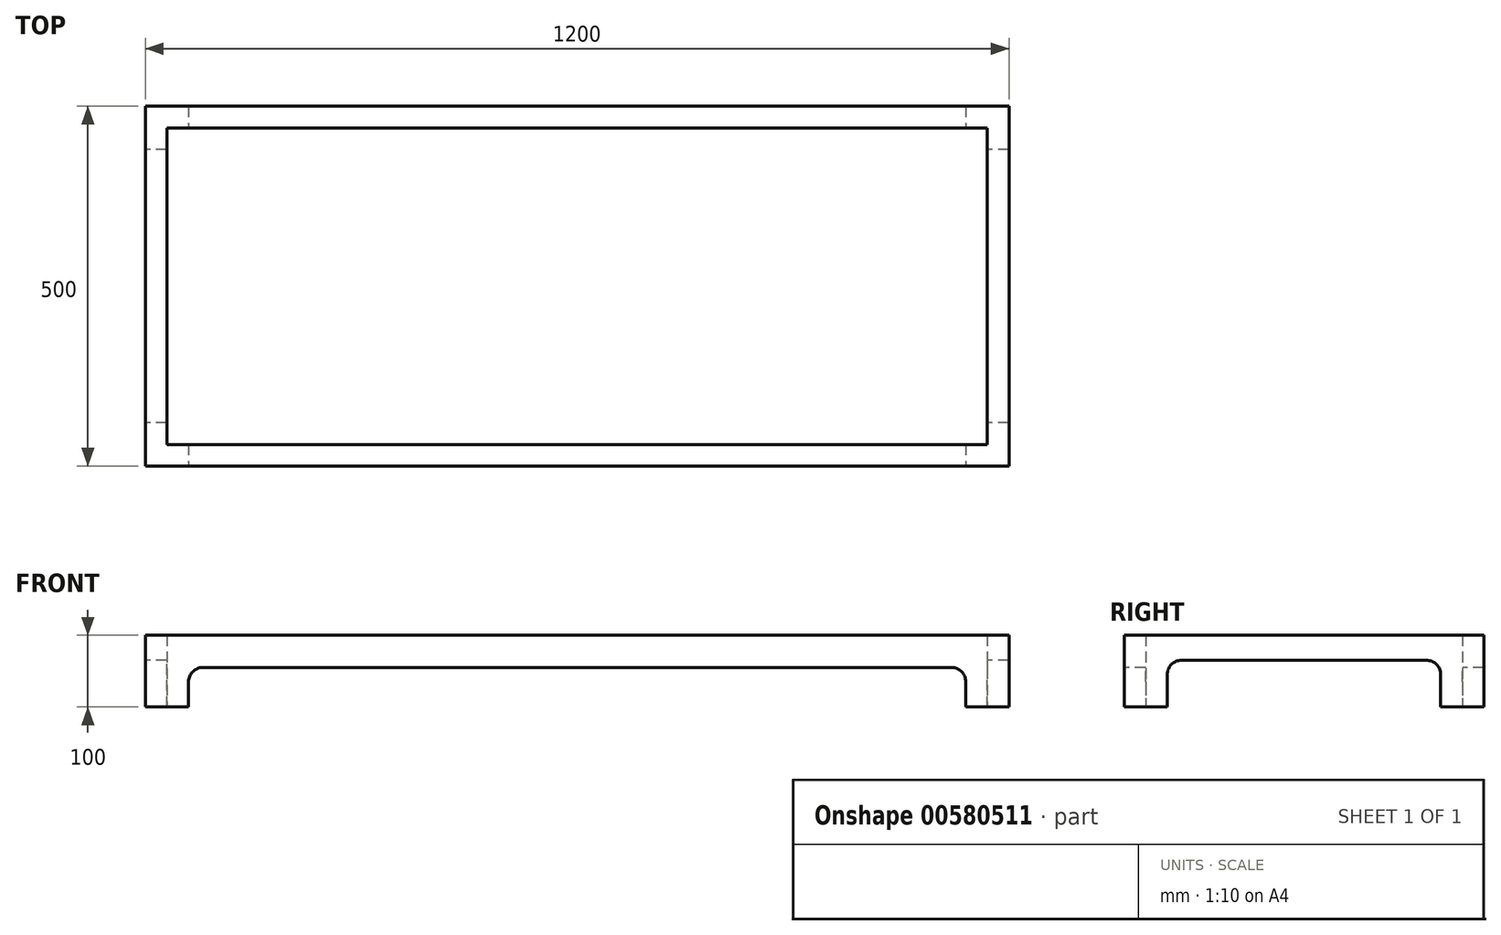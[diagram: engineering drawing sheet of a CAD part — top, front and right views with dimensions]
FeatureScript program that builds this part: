
annotation { "Feature Type Name" : "Feature", "Feature Type Description" : "" }
export const myFeature = defineFeature(function(context is Context, id is Id, definition is map)
    precondition{}
    {
        {
            var Q0;
            Q0=qCreatedBy(makeId("Top.planeOp"),FACE);
            var sketch = newSketch(context, id + "F0", { "sketchPlane" : qUnion([Q0])});
            skLineSegment(sketch, "E0.bottom", {"start": v(0, 0) * mm, "end": v(1200, 0) * mm});
            skLineSegment(sketch, "E0.top", {"start": v(0, 500) * mm, "end": v(1200, 500) * mm});
            skLineSegment(sketch, "E0.left", {"start": v(0, 0) * mm, "end": v(0, 500) * mm});
            skLineSegment(sketch, "E0.right", {"start": v(1200, 0) * mm, "end": v(1200, 500) * mm});
            skLineSegment(sketch, "E1.0", {"start": v(30, 470) * mm, "end": v(1170, 470) * mm});
            skLineSegment(sketch, "E1.1", {"start": v(30, 30) * mm, "end": v(30, 470) * mm});
            skLineSegment(sketch, "E1.2", {"start": v(30, 30) * mm, "end": v(1170, 30) * mm});
            skLineSegment(sketch, "E1.3", {"start": v(1170, 30) * mm, "end": v(1170, 470) * mm});
            skSolve(sketch);
        }
        {
            var Q0;
            Q0 = qSketchRegion(id + "F0", true);
            extrude(context, id + "F1", {"entities" : qUnion([Q0]), "depth" : 100 * mm, "offsetDistance" : 25 * mm});
        }
        {
            var Q0;
            Q0=makeQuery(id+"F1.opExtrude","SWEPT_FACE",FACE,{"disambiguationData":[OSD([sQuery(id+"F0.wireOp",EDGE,"E0.bottom")])]});
            var sketch = newSketch(context, id + "F2", { "sketchPlane" : qUnion([Q0])});
            skLineSegment(sketch, "E2.bottom", {"start": v(60, 0) * mm, "end": v(1140, 0) * mm});
            skLineSegment(sketch, "E2.top", {"start": v(80, 55) * mm, "end": v(1120, 55) * mm});
            skLineSegment(sketch, "E2.left", {"start": v(60, 0) * mm, "end": v(60, 35) * mm});
            skLineSegment(sketch, "E2.right", {"start": v(1140, 0) * mm, "end": v(1140, 35) * mm});
            skPoint(sketch, "E3.visualSharp", {"position": v(60, 55) * mm});
            skArc(sketch, "E3.filletArc", {"start": v(80, 55) * mm, "mid": v(65.86, 49.14) * mm, "end": v(60, 35) * mm});
            skPoint(sketch, "E4.visualSharp", {"position": v(1140, 55) * mm});
            skArc(sketch, "E4.filletArc", {"start": v(1140, 35) * mm, "mid": v(1134.14, 49.14) * mm, "end": v(1120, 55) * mm});
            skSolve(sketch);
        }
        {
            var Q0;
            Q0 = qSketchRegion(id + "F2", true);
            extrude(context, id + "F3", {"entities" : qUnion([Q0]), "operationType" : NewBodyOperationType.REMOVE, "endBound" : BoundingType.THROUGH_ALL, "oppositeDirection" : true, "depth" : 25 * mm, "offsetDistance" : 25 * mm});
        }
        {
            var Q0;
            Q0=makeQuery(id+"F1.opExtrude","SWEPT_FACE",FACE,{"disambiguationData":[OSD([sQuery(id+"F0.wireOp",EDGE,"E0.left")])]});
            var sketch = newSketch(context, id + "F4", { "sketchPlane" : qUnion([Q0])});
            skLineSegment(sketch, "E5.bottom", {"start": v(-440, 0) * mm, "end": v(-60, 0) * mm});
            skLineSegment(sketch, "E5.top", {"start": v(-420, 65) * mm, "end": v(-80, 65) * mm});
            skLineSegment(sketch, "E5.left", {"start": v(-440, 0) * mm, "end": v(-440, 45) * mm});
            skLineSegment(sketch, "E5.right", {"start": v(-60, 0) * mm, "end": v(-60, 45) * mm});
            skPoint(sketch, "E6.visualSharp", {"position": v(-440, 65) * mm});
            skArc(sketch, "E6.filletArc", {"start": v(-420, 65) * mm, "mid": v(-434.14, 59.14) * mm, "end": v(-440, 45) * mm});
            skPoint(sketch, "E7.visualSharp", {"position": v(-60, 65) * mm});
            skArc(sketch, "E7.filletArc", {"start": v(-60, 45) * mm, "mid": v(-65.86, 59.14) * mm, "end": v(-80, 65) * mm});
            skSolve(sketch);
        }
        {
            var Q0;
            Q0 = qSketchRegion(id + "F4", true);
            extrude(context, id + "F5", {"entities" : qUnion([Q0]), "operationType" : NewBodyOperationType.REMOVE, "endBound" : BoundingType.THROUGH_ALL, "oppositeDirection" : true, "depth" : 25 * mm, "offsetDistance" : 25 * mm});
        }
    });
